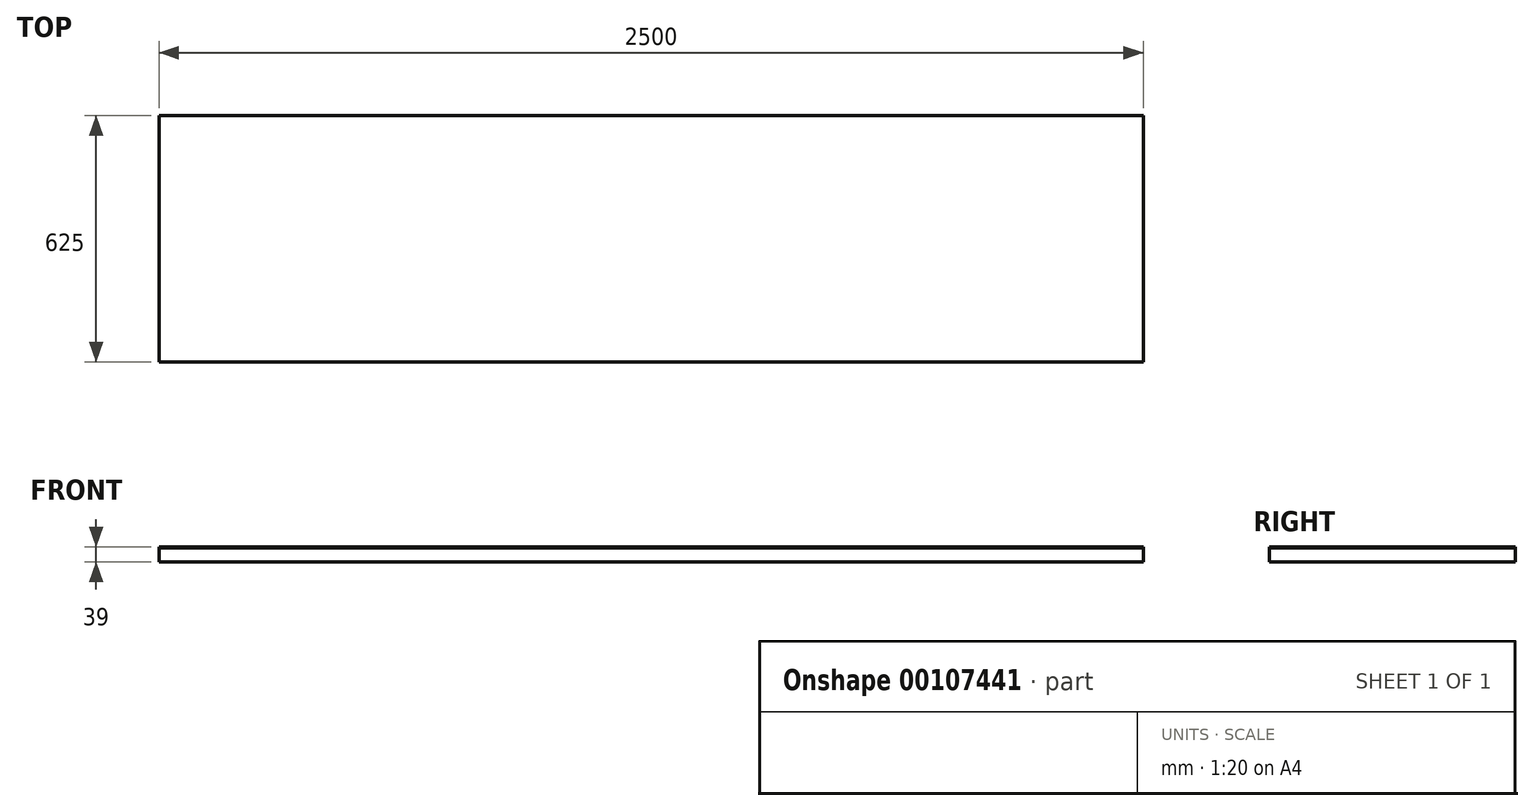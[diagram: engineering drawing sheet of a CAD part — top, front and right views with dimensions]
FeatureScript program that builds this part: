
annotation { "Feature Type Name" : "Feature", "Feature Type Description" : "" }
export const myFeature = defineFeature(function(context is Context, id is Id, definition is map)
    precondition{}
    {
        {
            var Q0;
            Q0=qCreatedBy(makeId("Top.planeOp"),FACE);
            var sketch = newSketch(context, id + "F0", { "sketchPlane" : qUnion([Q0])});
            skLineSegment(sketch, "E0.bottom", {"start": v(0, 0) * mm, "end": v(2500, 0) * mm});
            skLineSegment(sketch, "E0.top", {"start": v(0, 625) * mm, "end": v(2500, 625) * mm});
            skLineSegment(sketch, "E0.left", {"start": v(0, 0) * mm, "end": v(0, 625) * mm});
            skLineSegment(sketch, "E0.right", {"start": v(2500, 0) * mm, "end": v(2500, 625) * mm});
            skSolve(sketch);
        }
        {
            var Q0;
            Q0=makeQuery(id+"F0.imprint","IMPRINT",FACE,{"disambiguationData":[TD([[makeQuery(id+"F0.imprint","IMPRINT",EDGE,{"derivedFrom":sQuery(id+"F0.wireOp",EDGE,"E0.bottom")}),1.0]])]});
            extrude(context, id + "F1", {"entities" : qUnion([Q0]), "depth" : 3 * mm});
        }
        {
            var Q0;
            Q0=makeQuery(id+"F1.opExtrude","CAP_FACE",FACE,{"disambiguationData":[OSD([sQuery(id+"F0.wireOp",EDGE,"E0.bottom"),sQuery(id+"F0.wireOp",EDGE,"E0.top"),sQuery(id+"F0.wireOp",EDGE,"E0.left"),sQuery(id+"F0.wireOp",EDGE,"E0.right")])],"isStart":true});
            extrude(context, id + "F2", {"entities" : qUnion([Q0]), "depth" : 36 * mm});
        }
    });
